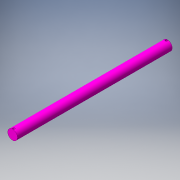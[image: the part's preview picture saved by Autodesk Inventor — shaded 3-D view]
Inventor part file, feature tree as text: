
AUTODESK INVENTOR PART (.ipt)
format: ipt  version: 2016 (Build 200138000, 138)  size: 104,448 bytes
history: native  units: in
note: dims shown in document units (in); Inventor stores cm internally (conversion verified against a paired STEP export)
features: extrude x2, sketch x2
ambient origin geometry x8: Origin, YZ Plane, XZ Plane, XY Plane, X Axis, Y Axis, Z Axis, Center Point
bodies: Solid1 (feature_tree)
feature tree (4):
  extrude  "Extrusion1"  Depth=8.0in TaperAngle=0.0deg
  extrude  "Extrusion4"  Depth=0.06in
  sketch  "Sketch1"  dims[d0=0.5in d1=8.0in d2=0.0in]
  sketch  "Sketch4"  dims[d13=0.06in d15=0.06in d16=0.1in d17=0.6in d18=0.0in d19=0.1in]
